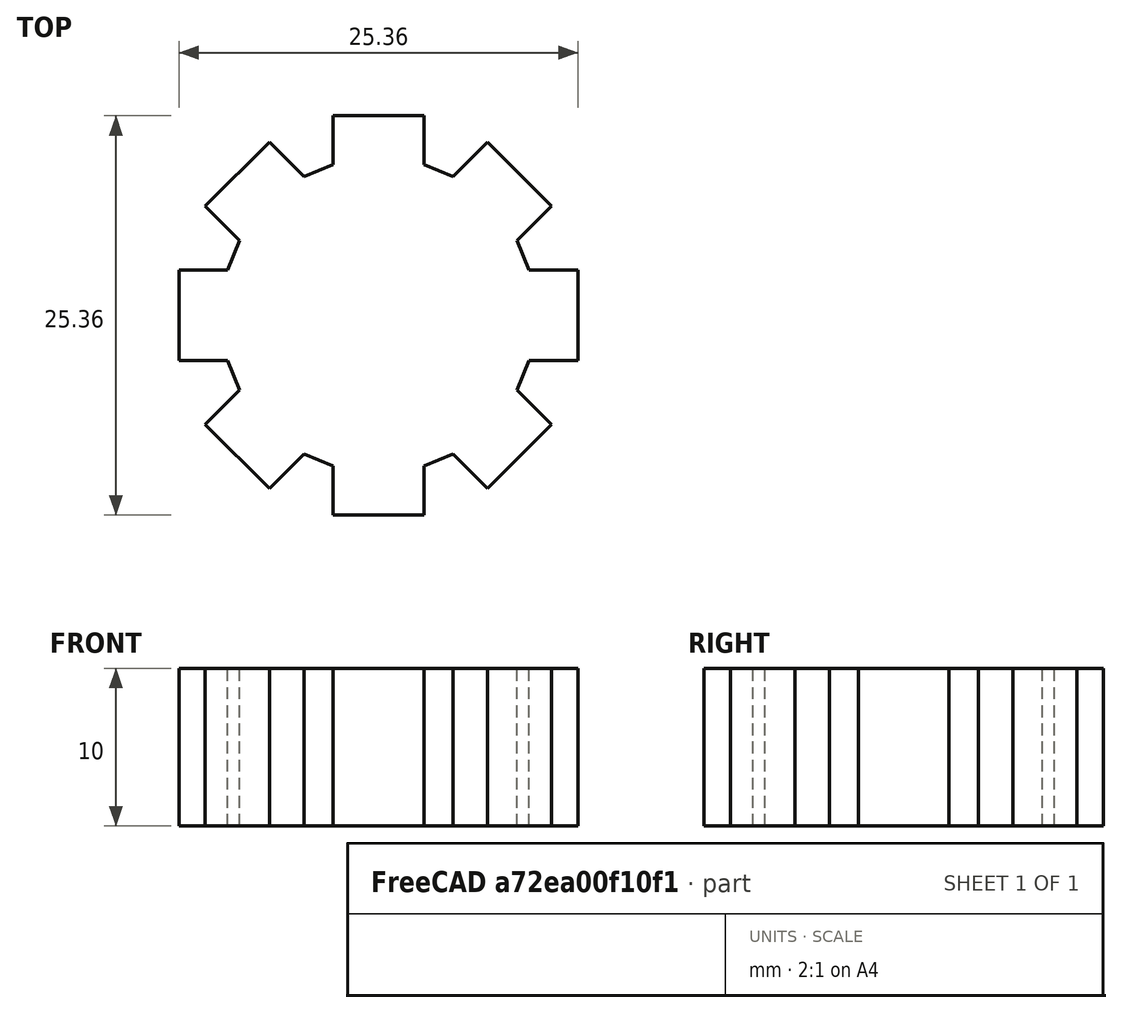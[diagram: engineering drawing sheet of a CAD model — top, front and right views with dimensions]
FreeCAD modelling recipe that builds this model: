
FCSTD DOCUMENT  (FreeCAD 0.17RUnknown)
Label: gear2
License: All rights reserved
LicenseURL: http://en.wikipedia.org/wiki/All_rights_reserved
objects: Sketcher::SketchObject×1, PartDesign::Pad×1, PartDesign::Body×1
note: 4 computed .brp shape members not serialized (recipe doc carries the construction recipe); baked Part::Feature solids carry a one-line shape summary decoded from their .brp

FEATURE [Sketcher::SketchObject] Sketch
  MapMode = 5
  sketch-geometry (38):
    g0: LineSegment StartX=0 StartY=12.6761 StartZ=0 EndX=2.88377 EndY=12.6761 EndZ=0
    g1: LineSegment StartX=2.88377 StartY=12.6761 StartZ=0 EndX=2.88377 EndY=9.57517 EndZ=0
    g2: LineSegment StartX=2.88377 StartY=9.57517 StartZ=0 EndX=4.73153 EndY=8.8098 EndZ=0
    g3: LineSegment StartX=4.73153 StartY=8.8098 StartZ=0 EndX=6.92423 EndY=11.0025 EndZ=0
    g4: LineSegment StartX=6.92423 StartY=11.0025 StartZ=0 EndX=11.0025 EndY=6.92423 EndZ=0
    g5: LineSegment StartX=11.0025 StartY=6.92423 StartZ=0 EndX=8.8098 EndY=4.73153 EndZ=0
    g6: LineSegment StartX=8.8098 StartY=4.73153 StartZ=0 EndX=9.57517 EndY=2.88377 EndZ=0
    g7: LineSegment StartX=9.57517 StartY=2.88377 StartZ=0 EndX=12.6761 EndY=2.88377 EndZ=0
    g8: LineSegment StartX=12.6761 StartY=2.88377 StartZ=0 EndX=12.6761 EndY=0 EndZ=0
    g9: ArcOfCircle [constr] CenterX=0 CenterY=0 CenterZ=0 NormalX=0 NormalY=0 NormalZ=1 AngleXU=0 Radius=10 StartAngle=0 EndAngle=1.5708
    g10: ArcOfCircle [constr] CenterX=0 CenterY=0 CenterZ=0 NormalX=0 NormalY=0 NormalZ=1 AngleXU=0 Radius=13 StartAngle=0 EndAngle=1.5708
    g11: LineSegment StartX=12.6761 StartY=0 StartZ=0 EndX=12.6761 EndY=-2.88377 EndZ=0
    g12: LineSegment StartX=12.6761 StartY=-2.88377 StartZ=0 EndX=9.57517 EndY=-2.88377 EndZ=0
    g13: LineSegment StartX=9.57517 StartY=-2.88377 StartZ=0 EndX=8.8098 EndY=-4.73153 EndZ=0
    g14: LineSegment StartX=8.8098 StartY=-4.73153 StartZ=0 EndX=11.0025 EndY=-6.92423 EndZ=0
    g15: LineSegment StartX=11.0025 StartY=-6.92423 StartZ=0 EndX=6.92423 EndY=-11.0025 EndZ=0
    g16: LineSegment StartX=6.92423 StartY=-11.0025 StartZ=0 EndX=4.73153 EndY=-8.8098 EndZ=0
    g17: LineSegment StartX=4.73153 StartY=-8.8098 StartZ=0 EndX=2.88377 EndY=-9.57517 EndZ=0
    g18: LineSegment StartX=2.88377 StartY=-9.57517 StartZ=0 EndX=2.88377 EndY=-12.6761 EndZ=0
    g19: LineSegment StartX=2.88377 StartY=-12.6761 StartZ=0 EndX=0 EndY=-12.6761 EndZ=0
    g20: LineSegment StartX=0 StartY=12.6761 StartZ=0 EndX=-2.88377 EndY=12.6761 EndZ=0
    g21: LineSegment StartX=-2.88377 StartY=12.6761 StartZ=0 EndX=-2.88377 EndY=9.57517 EndZ=0
    g22: LineSegment StartX=-2.88377 StartY=9.57517 StartZ=0 EndX=-4.73153 EndY=8.8098 EndZ=0
    g23: LineSegment StartX=-4.73153 StartY=8.8098 StartZ=0 EndX=-6.92423 EndY=11.0025 EndZ=0
    g24: LineSegment StartX=-6.92423 StartY=11.0025 StartZ=0 EndX=-11.0025 EndY=6.92423 EndZ=0
    g25: LineSegment StartX=-11.0025 StartY=6.92423 StartZ=0 EndX=-8.8098 EndY=4.73153 EndZ=0
    g26: LineSegment StartX=-8.8098 StartY=4.73153 StartZ=0 EndX=-9.57517 EndY=2.88377 EndZ=0
    g27: LineSegment StartX=-9.57517 StartY=2.88377 StartZ=0 EndX=-12.6761 EndY=2.88377 EndZ=0
    g28: LineSegment StartX=-12.6761 StartY=2.88377 StartZ=0 EndX=-12.6761 EndY=0 EndZ=0
    g29: LineSegment StartX=-12.6761 StartY=0 StartZ=0 EndX=-12.6761 EndY=-2.88377 EndZ=0
    g30: LineSegment StartX=-12.6761 StartY=-2.88377 StartZ=0 EndX=-9.57517 EndY=-2.88377 EndZ=0
    g31: LineSegment StartX=-9.57517 StartY=-2.88377 StartZ=0 EndX=-8.8098 EndY=-4.73153 EndZ=0
    g32: LineSegment StartX=-8.8098 StartY=-4.73153 StartZ=0 EndX=-11.0025 EndY=-6.92423 EndZ=0
    g33: LineSegment StartX=-11.0025 StartY=-6.92423 StartZ=0 EndX=-6.92423 EndY=-11.0025 EndZ=0
    g34: LineSegment StartX=-6.92423 StartY=-11.0025 StartZ=0 EndX=-4.73153 EndY=-8.8098 EndZ=0
    g35: LineSegment StartX=-4.73153 StartY=-8.8098 StartZ=0 EndX=-2.88377 EndY=-9.57517 EndZ=0
    g36: LineSegment StartX=-2.88377 StartY=-9.57517 StartZ=0 EndX=-2.88377 EndY=-12.6761 EndZ=0
    g37: LineSegment StartX=-2.88377 StartY=-12.6761 StartZ=0 EndX=0 EndY=-12.6761 EndZ=0
  constraints (94):
    c: Coincident(g0,g1)
    c: Coincident(g1,g2)
    c: Coincident(g2,g3)
    c: Coincident(g3,g4)
    c: Coincident(g4,g5)
    c: Coincident(g5,g6)
    c: Coincident(g7,g8)
    c: Perpendicular(g1,g0)
    c: Perpendicular(g4,g3)
    c: Perpendicular(g4,g5)
    c: Perpendicular(g-2,g0)
    c: Perpendicular(g-1,g8)
    c: PointOnObject(g0,g-2)
    c: PointOnObject(g8,g-1)
    c: Perpendicular(g8,g7)
    c: Distance(g2) = 2
    c: Distance(g6) = 2
    c: Coincident(g9,g-1)
    c: PointOnObject(g9,g-1)
    c: PointOnObject(g9,g-2)
    c: Radius(g9) = 10
    c: PointOnObject(g7,g9)
    c: PointOnObject(g6,g9)
    c: PointOnObject(g5,g9)
    c: PointOnObject(g2,g9)
    c: PointOnObject(g1,g9)
    c: Coincident(g10,g-1)
    c: PointOnObject(g10,g-1)
    c: PointOnObject(g10,g-2)
    c: Radius(g10) = 13
    c: PointOnObject(g7,g10)
    c: PointOnObject(g4,g10)
    c: PointOnObject(g3,g10)
    c: PointOnObject(g0,g10)
    c: Coincident(g8,g11)
    c: Coincident(g11,g12)
    c: Horizontal(g12)
    c: Coincident(g13,g14)
    c: Coincident(g14,g15)
    c: Coincident(g15,g16)
    c: Coincident(g16,g17)
    c: Coincident(g17,g18)
    c: Coincident(g18,g19)
    c: Symmetric(g7,g11,g-1)
    c: Symmetric(g7,g12,g-1)
    c: Symmetric(g6,g13,g-1)
    c: Symmetric(g13,g5,g-1)
    c: Symmetric(g14,g4,g-1)
    c: Symmetric(g15,g3,g-1)
    c: Symmetric(g2,g16,g-1)
    c: Symmetric(g17,g1,g-1)
    c: Symmetric(g18,g0,g-1)
    c: PointOnObject(g19,g-2)
    c: Perpendicular(g-2,g19)
    c: Coincident(g0,g20)
    c: Coincident(g20,g21)
    c: Coincident(g21,g22)
    c: Coincident(g22,g23)
    c: Coincident(g23,g24)
    c: Coincident(g24,g25)
    c: Coincident(g25,g26)
    c: Coincident(g27,g28)
    c: PointOnObject(g28,g-1)
    c: Symmetric(g0,g20,g-2)
    c: Symmetric(g1,g21,g-2)
    c: Symmetric(g22,g2,g-2)
    c: Symmetric(g23,g3,g-2)
    c: Symmetric(g24,g4,g-2)
    c: Symmetric(g5,g25,g-2)
    c: Symmetric(g26,g6,g-2)
    c: Symmetric(g27,g7,g-2)
    c: Symmetric(g27,g7,g-2)
    c: Perpendicular(g28,g-1)
    c: Coincident(g28,g29)
    c: Coincident(g29,g30)
    c: Coincident(g31,g32)
    c: Coincident(g32,g33)
    c: Coincident(g33,g34)
    c: Coincident(g34,g35)
    c: Coincident(g35,g36)
    c: Coincident(g36,g37)
    c: Coincident(g37,g19)
    c: Symmetric(g29,g7,g-1)
    c: Symmetric(g30,g7,g-1)
    c: Symmetric(g31,g6,g-1)
    c: Symmetric(g31,g5,g-1)
    c: Symmetric(g32,g4,g-1)
    c: Symmetric(g33,g3,g-1)
    c: Symmetric(g34,g2,g-1)
    c: Symmetric(g35,g1,g-1)
    c: Symmetric(g36,g0,g-1)
    c: Coincident(g6,g7)
    c: Angle(g2,g1) = 1.9635
    c: Angle(g6,g5) = 1.9635
FEATURE [PartDesign::Pad] Pad
  Length = 10
  Length2 = 100
  Profile = -> Sketch
  Type = 0
FEATURE [PartDesign::Body] Body
  Group = -> [Sketch,Pad]
  Origin = -> Origin
  Tip = -> Pad
